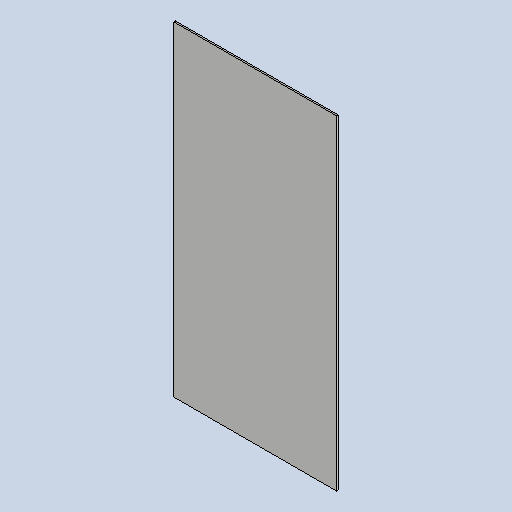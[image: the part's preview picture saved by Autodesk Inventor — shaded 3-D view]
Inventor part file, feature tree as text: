
AUTODESK INVENTOR PART (.ipt)
format: ipt  version: 2025 (Build 290162010, 162A)  size: 99,328 bytes
history: native  units: mm
features: other x2, sheet_metal_op x1, sketch x1
ambient origin geometry x8: Origin, YZ Plane, XZ Plane, XY Plane, X Axis, Y Axis, Z Axis, Center Point
bodies: Body1 (feature_tree)
feature tree (4):
  sheet_metal_op  "Face2"
  sketch  "Sketch1"  dims[d0=400.0mm d1=200.2mm d3=2.0mm]
  other  "Plate2"
  other  "Definition1"
